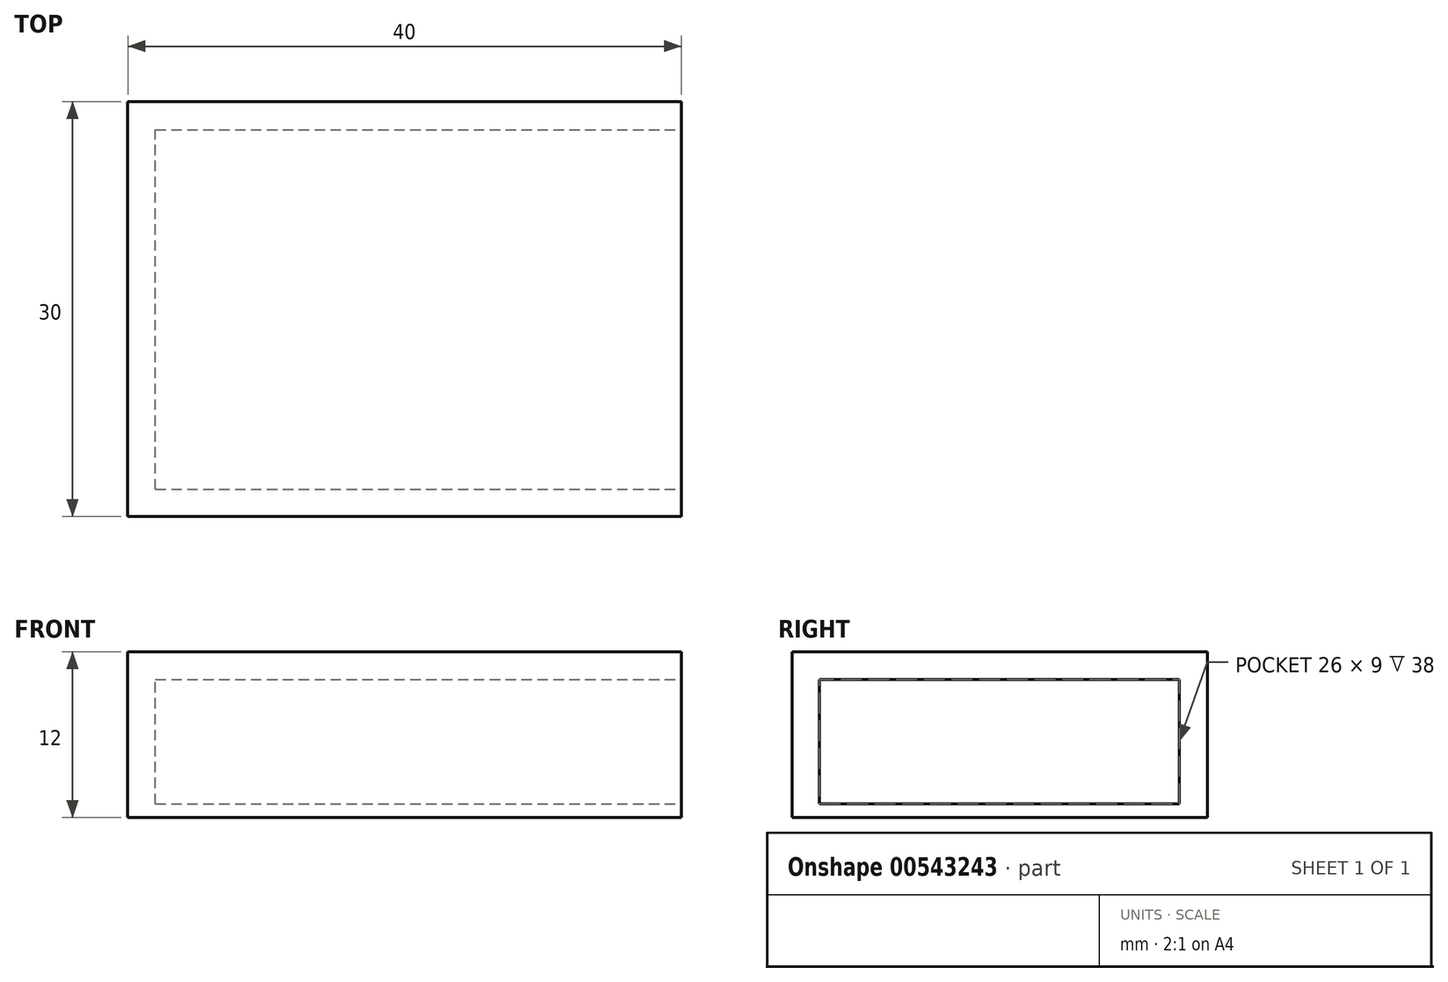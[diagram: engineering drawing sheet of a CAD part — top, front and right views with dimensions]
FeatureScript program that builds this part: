
annotation { "Feature Type Name" : "Feature", "Feature Type Description" : "" }
export const myFeature = defineFeature(function(context is Context, id is Id, definition is map)
    precondition{}
    {
        {
            var Q0;
            Q0=qCreatedBy(makeId("Top.planeOp"),FACE);
            var sketch = newSketch(context, id + "F0", { "sketchPlane" : qUnion([Q0])});
            skLineSegment(sketch, "E0.bottom", {"start": v(-21.15, -3) * mm, "end": v(18.85, -3) * mm});
            skLineSegment(sketch, "E0.top", {"start": v(-21.15, 27) * mm, "end": v(18.85, 27) * mm});
            skLineSegment(sketch, "E0.left", {"start": v(-21.15, -3) * mm, "end": v(-21.15, 27) * mm});
            skLineSegment(sketch, "E0.right", {"start": v(18.85, -3) * mm, "end": v(18.85, 27) * mm});
            skSolve(sketch);
        }
        {
            var Q0;
            Q0=makeQuery(id+"F0.imprint","IMPRINT",FACE,{"disambiguationData":[TD([[makeQuery(id+"F0.imprint","IMPRINT",EDGE,{"derivedFrom":sQuery(id+"F0.wireOp",EDGE,"E0.bottom")}),1.0]])]});
            var Q1;
            Q1 = qSketchRegion(id + "F2", true);
            extrude(context, id + "F1", {"entities" : qUnion([Q0, Q1]), "depth" : 12 * mm, "offsetDistance" : 25 * mm});
        }
        {
            var Q0;
            Q0=makeQuery(id+"F1.opExtrude","SWEPT_FACE",FACE,{"disambiguationData":[OSD([sQuery(id+"F0.wireOp",EDGE,"E0.right")])]});
            var sketch = newSketch(context, id + "F2", { "sketchPlane" : qUnion([Q0])});
            skLineSegment(sketch, "E1.bottom", {"start": v(-1.03, 1) * mm, "end": v(24.97, 1) * mm});
            skLineSegment(sketch, "E1.top", {"start": v(-1.03, 10) * mm, "end": v(24.97, 10) * mm});
            skLineSegment(sketch, "E1.left", {"start": v(-1.03, 1) * mm, "end": v(-1.03, 10) * mm});
            skLineSegment(sketch, "E1.right", {"start": v(24.97, 1) * mm, "end": v(24.97, 10) * mm});
            skSolve(sketch);
        }
        {
            var Q0;
            Q0=makeQuery(id+"F2.imprint","IMPRINT",FACE,{"disambiguationData":[TD([[makeQuery(id+"F2.imprint","IMPRINT",EDGE,{"derivedFrom":sQuery(id+"F2.wireOp",EDGE,"E1.bottom")}),1.0]])]});
            extrude(context, id + "F3", {"entities" : qUnion([Q0]), "operationType" : NewBodyOperationType.REMOVE, "oppositeDirection" : true, "depth" : 38 * mm, "offsetDistance" : 25 * mm});
        }
    });
